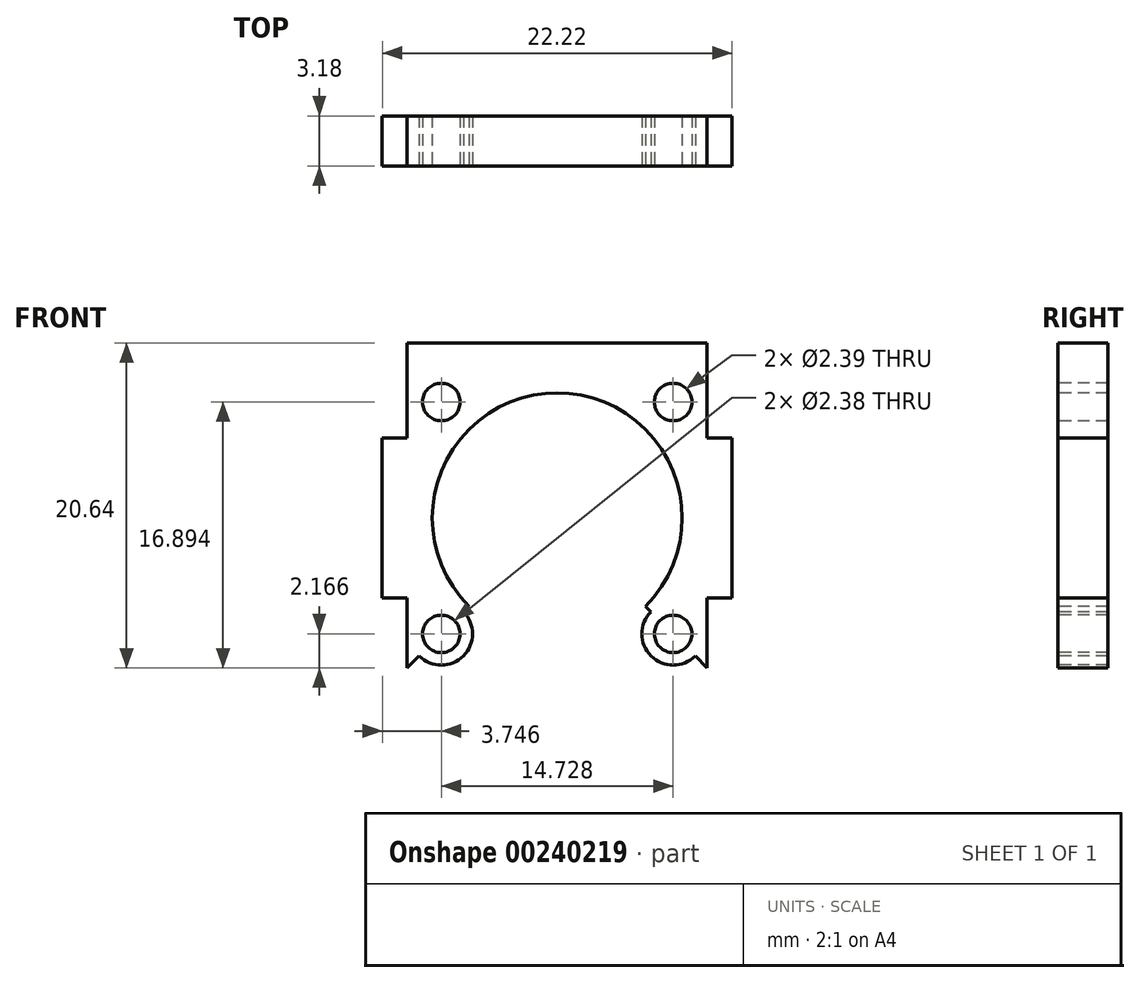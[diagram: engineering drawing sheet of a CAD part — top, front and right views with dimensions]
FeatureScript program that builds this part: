
annotation { "Feature Type Name" : "Feature", "Feature Type Description" : "" }
export const myFeature = defineFeature(function(context is Context, id is Id, definition is map)
    precondition{}
    {
        {
            var Q0;
            Q0=qCreatedBy(makeId("Front.planeOp"),FACE);
            var sketch = newSketch(context, id + "F0", { "sketchPlane" : qUnion([Q0])});
            skCircle(sketch, "E0", {"center": v(0, 0) * mm, "radius": 7.94 * mm});
            skCircle(sketch, "E1", {"center": v(0, 0) * mm, "radius": 9.53 * mm, "construction": true});
            skLineSegment(sketch, "E2.bottom", {"start": v(-9.53, 9.53) * mm, "end": v(9.52, 9.53) * mm, "construction": true});
            skLineSegment(sketch, "E2.top", {"start": v(-9.53, -9.53) * mm, "end": v(9.52, -9.53) * mm, "construction": true});
            skLineSegment(sketch, "E2.left", {"start": v(-9.53, 9.53) * mm, "end": v(-9.53, -9.53) * mm});
            skLineSegment(sketch, "E2.right", {"start": v(9.53, 9.53) * mm, "end": v(9.53, -9.53) * mm});
            skLineSegment(sketch, "E3.bottom", {"start": v(-9.52, 9.53) * mm, "end": v(9.52, 9.53) * mm, "construction": true});
            skLineSegment(sketch, "E3.top", {"start": v(-9.53, 11.11) * mm, "end": v(9.52, 11.11) * mm});
            skLineSegment(sketch, "E3.left", {"start": v(-9.53, 9.53) * mm, "end": v(-9.53, 11.11) * mm});
            skLineSegment(sketch, "E3.right", {"start": v(9.52, 9.53) * mm, "end": v(9.52, 11.11) * mm});
            skLineSegment(sketch, "E4.bottom", {"start": v(-9.52, -9.53) * mm, "end": v(9.52, -9.53) * mm, "construction": true});
            skLineSegment(sketch, "E4.top", {"start": v(-9.52, -11.11) * mm, "end": v(9.52, -11.11) * mm});
            skLineSegment(sketch, "E4.left", {"start": v(-9.53, -9.53) * mm, "end": v(-9.53, -11.11) * mm});
            skLineSegment(sketch, "E4.right", {"start": v(9.52, -9.53) * mm, "end": v(9.52, -11.11) * mm});
            skLineSegment(sketch, "E5.bottom", {"start": v(-9.53, 5.08) * mm, "end": v(-7.94, 5.08) * mm});
            skLineSegment(sketch, "E5.top", {"start": v(-9.53, -5.08) * mm, "end": v(-7.94, -5.08) * mm});
            skLineSegment(sketch, "E5.left", {"start": v(-9.53, 5.08) * mm, "end": v(-9.53, -5.08) * mm});
            skLineSegment(sketch, "E5.right", {"start": v(-7.94, 5.08) * mm, "end": v(-7.94, -5.08) * mm});
            skPoint(sketch, "E6.firstSnap0", {"position": v(-8.73, 5.08) * mm});
            skPoint(sketch, "E6.oppositeSnap0", {"position": v(-8.73, -5.08) * mm});
            skLineSegment(sketch, "E6.bottom", {"start": v(9.53, 5.08) * mm, "end": v(7.94, 5.08) * mm});
            skLineSegment(sketch, "E6.top", {"start": v(9.53, -5.08) * mm, "end": v(7.94, -5.08) * mm});
            skLineSegment(sketch, "E6.left", {"start": v(9.53, 5.08) * mm, "end": v(9.53, -5.08) * mm});
            skLineSegment(sketch, "E6.right", {"start": v(7.94, 5.08) * mm, "end": v(7.94, -5.08) * mm});
            skLineSegment(sketch, "E7.bottom", {"start": v(-9.53, 5.08) * mm, "end": v(-11.11, 5.08) * mm});
            skLineSegment(sketch, "E7.top", {"start": v(-9.53, -5.08) * mm, "end": v(-11.11, -5.08) * mm});
            skLineSegment(sketch, "E7.right", {"start": v(-11.11, 5.08) * mm, "end": v(-11.11, -5.08) * mm});
            skLineSegment(sketch, "E8.bottom", {"start": v(9.53, 5.08) * mm, "end": v(11.11, 5.08) * mm});
            skLineSegment(sketch, "E8.top", {"start": v(9.53, -5.08) * mm, "end": v(11.11, -5.08) * mm});
            skLineSegment(sketch, "E8.right", {"start": v(11.11, 5.08) * mm, "end": v(11.11, -5.08) * mm});
            skLineSegment(sketch, "E9", {"start": v(0, 0) * mm, "end": v(-9.53, -9.53) * mm, "construction": true});
            skLineSegment(sketch, "E10", {"start": v(0, 0) * mm, "end": v(9.52, -9.53) * mm, "construction": true});
            skLineSegment(sketch, "E11", {"start": v(0, 0) * mm, "end": v(9.52, 9.52) * mm, "construction": true});
            skLineSegment(sketch, "E12", {"start": v(0, 0) * mm, "end": v(-9.52, 9.53) * mm, "construction": true});
            skCircle(sketch, "E13", {"center": v(-7.36, -7.36) * mm, "radius": 1.2 * mm});
            skCircle(sketch, "E14", {"center": v(7.36, -7.36) * mm, "radius": 1.2 * mm});
            skCircle(sketch, "E15", {"center": v(-7.36, -7.36) * mm, "radius": 1.98 * mm});
            skCircle(sketch, "E16", {"center": v(7.36, -7.36) * mm, "radius": 1.98 * mm});
            skLineSegment(sketch, "E17", {"start": v(-5.61, -5.61) * mm, "end": v(-9.53, -9.53) * mm});
            skLineSegment(sketch, "E18", {"start": v(5.61, -5.61) * mm, "end": v(9.52, -9.53) * mm});
            skLineSegment(sketch, "E19", {"start": v(-7.36, -7.36) * mm, "end": v(-9.53, -5.2) * mm});
            skLineSegment(sketch, "E20", {"start": v(7.36, -7.36) * mm, "end": v(9.53, -5.2) * mm});
            skLineSegment(sketch, "E21", {"start": v(-3.56, -11.11) * mm, "end": v(-3.56, -9.4) * mm});
            skLineSegment(sketch, "E22", {"start": v(-3.56, -9.4) * mm, "end": v(3.56, -9.4) * mm});
            skLineSegment(sketch, "E23", {"start": v(3.56, -9.4) * mm, "end": v(3.56, -7.1) * mm});
            skCircle(sketch, "E24", {"center": v(-7.36, 7.36) * mm, "radius": 1.2 * mm});
            skCircle(sketch, "E25", {"center": v(7.36, 7.36) * mm, "radius": 1.2 * mm});
            skSolve(sketch);
        }
        {
            var Q0;
            Q0=makeQuery(id+"F0.imprint","IMPRINT",FACE,{"disambiguationData":[TD([[makeQuery(id+"F0.imprint","IMPRINT",EDGE,{"derivedFrom":sQuery(id+"F0.wireOp",EDGE,"E7.bottom")}),1.0]])]});
            var Q1;
            Q1=makeQuery(id+"F0.imprint","IMPRINT",FACE,{"disambiguationData":[TD([[makeQuery(id+"F0.imprint","IMPRINT",EDGE,{"derivedFrom":sQuery(id+"F0.wireOp",EDGE,"E8.bottom")}),-1.0]])]});
            var Q2;
            {var subQ3=sQuery(id+"F0.wireOp",EDGE,"E19");var subQ5=sQuery(id+"F0.wireOp",EDGE,"E15");var subQ7=makeQuery(id+"F0.imprint","INTERSECT",VERTEX,{"derivedFrom":[subQ5,subQ3]});Q2=makeQuery(id+"F0.imprint","IMPRINT",FACE,{"disambiguationData":[TD([[makeQuery(id+"F0.imprint","IMPRINT",EDGE,{"disambiguationData":[TD([[subQ7,-1.0]])],"derivedFrom":subQ5}),-1.0]])]});}
            var Q3;
            {var subQ3=sQuery(id+"F0.wireOp",EDGE,"E20");var subQ5=sQuery(id+"F0.wireOp",EDGE,"E16");var subQ6=makeQuery(id+"F0.imprint","INTERSECT",VERTEX,{"derivedFrom":[subQ5,subQ3]});Q3=makeQuery(id+"F0.imprint","IMPRINT",FACE,{"disambiguationData":[TD([[makeQuery(id+"F0.imprint","IMPRINT",EDGE,{"disambiguationData":[TD([[subQ6,1.0]])],"derivedFrom":subQ5}),-1.0]])]});}
            var Q4;
            {var subQ3=sQuery(id+"F0.wireOp",EDGE,"E5.bottom");Q4=makeQuery(id+"F0.imprint","IMPRINT",FACE,{"disambiguationData":[TD([[makeQuery(id+"F0.imprint","IMPRINT",EDGE,{"derivedFrom":subQ3}),-1.0]])]});}
            var Q5;
            {var subQ3=sQuery(id+"F0.wireOp",EDGE,"E6.bottom");Q5=makeQuery(id+"F0.imprint","IMPRINT",FACE,{"disambiguationData":[TD([[makeQuery(id+"F0.imprint","IMPRINT",EDGE,{"derivedFrom":subQ3}),1.0]])]});}
            var Q6;
            Q6=makeQuery(id+"F0.imprint","IMPRINT",FACE,{"disambiguationData":[TD([[makeQuery(id+"F0.imprint","IMPRINT",EDGE,{"derivedFrom":sQuery(id+"F0.wireOp",EDGE,"E3.top")}),-1.0]])]});
            var Q7;
            {var subQ1=sQuery(id+"F0.wireOp",EDGE,"E5.top");Q7=makeQuery(id+"F0.imprint","IMPRINT",FACE,{"disambiguationData":[TD([[makeQuery(id+"F0.imprint","IMPRINT",EDGE,{"derivedFrom":subQ1}),-1.0]])]});}
            var Q8;
            {var subQ0=sQuery(id+"F0.wireOp",EDGE,"E6.top");Q8=makeQuery(id+"F0.imprint","IMPRINT",FACE,{"disambiguationData":[TD([[makeQuery(id+"F0.imprint","IMPRINT",EDGE,{"derivedFrom":subQ0}),1.0]])]});}
            var Q9;
            {var subQ0=sQuery(id+"F0.wireOp",EDGE,"E17");var subQ1=sQuery(id+"F0.wireOp",EDGE,"E13");var subQ2=makeQuery(id+"F0.imprint","INTERSECT",VERTEX,{"disambiguationData":[OD(0.0)],"derivedFrom":[subQ1,subQ0]});Q9=makeQuery(id+"F0.imprint","IMPRINT",FACE,{"disambiguationData":[TD([[makeQuery(id+"F0.imprint","IMPRINT",EDGE,{"disambiguationData":[TD([[subQ2,1.0]])],"derivedFrom":subQ1}),-1.0]])]});}
            var Q10;
            {var subQ0=sQuery(id+"F0.wireOp",EDGE,"E19");var subQ1=sQuery(id+"F0.wireOp",EDGE,"E13");var subQ2=makeQuery(id+"F0.imprint","INTERSECT",VERTEX,{"derivedFrom":[subQ1,subQ0]});Q10=makeQuery(id+"F0.imprint","IMPRINT",FACE,{"disambiguationData":[TD([[makeQuery(id+"F0.imprint","IMPRINT",EDGE,{"disambiguationData":[TD([[subQ2,-1.0]])],"derivedFrom":subQ1}),-1.0]])]});}
            var Q11;
            {var subQ0=sQuery(id+"F0.wireOp",EDGE,"E19");var subQ1=sQuery(id+"F0.wireOp",EDGE,"E13");var subQ2=makeQuery(id+"F0.imprint","INTERSECT",VERTEX,{"derivedFrom":[subQ1,subQ0]});Q11=makeQuery(id+"F0.imprint","IMPRINT",FACE,{"disambiguationData":[TD([[makeQuery(id+"F0.imprint","IMPRINT",EDGE,{"disambiguationData":[TD([[subQ2,1.0]])],"derivedFrom":subQ1}),-1.0]])]});}
            var Q12;
            {var subQ0=sQuery(id+"F0.wireOp",EDGE,"E18");var subQ1=sQuery(id+"F0.wireOp",EDGE,"E14");var subQ2=makeQuery(id+"F0.imprint","INTERSECT",VERTEX,{"disambiguationData":[OD(0.0)],"derivedFrom":[subQ1,subQ0]});Q12=makeQuery(id+"F0.imprint","IMPRINT",FACE,{"disambiguationData":[TD([[makeQuery(id+"F0.imprint","IMPRINT",EDGE,{"disambiguationData":[TD([[subQ2,1.0]])],"derivedFrom":subQ1}),-1.0]])]});}
            var Q13;
            {var subQ0=sQuery(id+"F0.wireOp",EDGE,"E20");var subQ1=sQuery(id+"F0.wireOp",EDGE,"E14");var subQ2=makeQuery(id+"F0.imprint","INTERSECT",VERTEX,{"derivedFrom":[subQ1,subQ0]});Q13=makeQuery(id+"F0.imprint","IMPRINT",FACE,{"disambiguationData":[TD([[makeQuery(id+"F0.imprint","IMPRINT",EDGE,{"disambiguationData":[TD([[subQ2,1.0]])],"derivedFrom":subQ1}),-1.0]])]});}
            var Q14;
            {var subQ0=sQuery(id+"F0.wireOp",EDGE,"E18");var subQ1=sQuery(id+"F0.wireOp",EDGE,"E14");var subQ2=makeQuery(id+"F0.imprint","INTERSECT",VERTEX,{"disambiguationData":[OD(0.0)],"derivedFrom":[subQ1,subQ0]});Q14=makeQuery(id+"F0.imprint","IMPRINT",FACE,{"disambiguationData":[TD([[makeQuery(id+"F0.imprint","IMPRINT",EDGE,{"disambiguationData":[TD([[subQ2,-1.0]])],"derivedFrom":subQ1}),-1.0]])]});}
            extrude(context, id + "F1", {"entities" : qUnion([Q0, Q1, Q2, Q3, Q4, Q5, Q6, Q7, Q8, Q9, Q10, Q11, Q12, Q13, Q14]), "oppositeDirection" : true, "depth" : 3.17 * mm});
        }
    });
